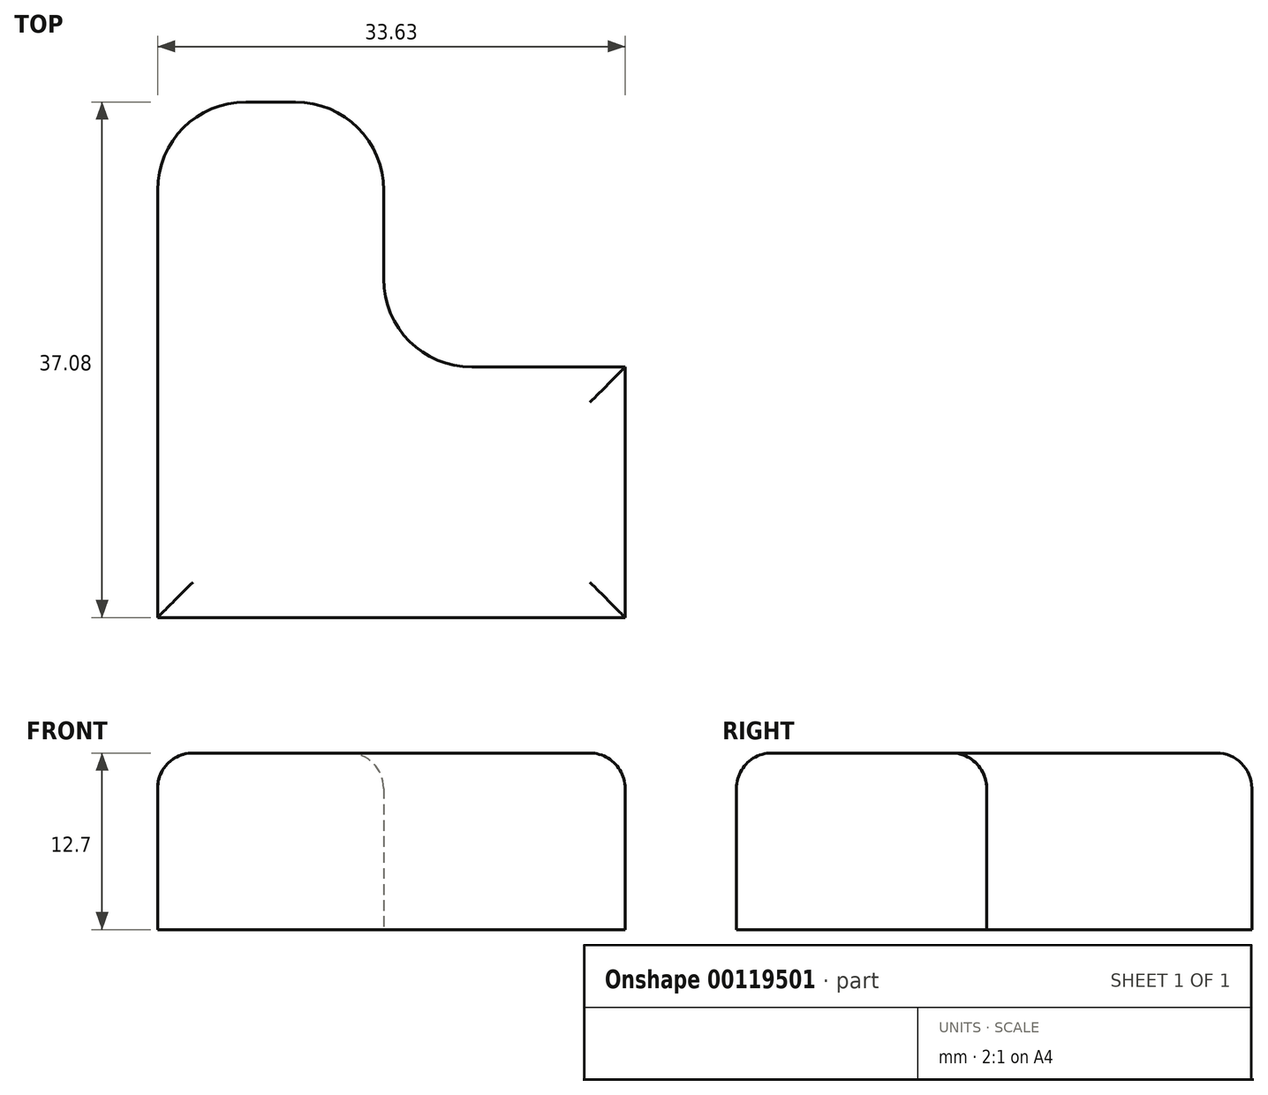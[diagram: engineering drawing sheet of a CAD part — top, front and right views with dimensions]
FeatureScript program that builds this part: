
annotation { "Feature Type Name" : "Feature", "Feature Type Description" : "" }
export const myFeature = defineFeature(function(context is Context, id is Id, definition is map)
    precondition{}
    {
        {
            var Q0;
            Q0=qCreatedBy(makeId("Top.planeOp"),FACE);
            var sketch = newSketch(context, id + "F0", { "sketchPlane" : qUnion([Q0])});
            skLineSegment(sketch, "E0", {"start": v(0, 0) * mm, "end": v(0, 30.73) * mm});
            skLineSegment(sketch, "E1", {"start": v(6.35, 37.08) * mm, "end": v(9.9, 37.08) * mm});
            skLineSegment(sketch, "E2", {"start": v(16.26, 30.73) * mm, "end": v(16.26, 24.36) * mm});
            skLineSegment(sketch, "E3", {"start": v(22.6, 18) * mm, "end": v(33.63, 18) * mm});
            skLineSegment(sketch, "E4", {"start": v(33.63, 18) * mm, "end": v(33.63, 0) * mm});
            skLineSegment(sketch, "E5", {"start": v(33.63, 0) * mm, "end": v(0, 0) * mm});
            skPoint(sketch, "E6.visualSharp", {"position": v(0, 37.08) * mm});
            skArc(sketch, "E6.filletArc", {"start": v(6.35, 37.08) * mm, "mid": v(1.86, 35.22) * mm, "end": v(0, 30.73) * mm});
            skPoint(sketch, "E7.visualSharp", {"position": v(16.26, 37.08) * mm});
            skArc(sketch, "E7.filletArc", {"start": v(16.26, 30.73) * mm, "mid": v(14.4, 35.22) * mm, "end": v(9.9, 37.08) * mm});
            skPoint(sketch, "E8.visualSharp", {"position": v(16.26, 18) * mm});
            skArc(sketch, "E8.filletArc", {"start": v(16.26, 24.36) * mm, "mid": v(18.12, 19.87) * mm, "end": v(22.6, 18) * mm});
            skSolve(sketch);
        }
        {
            var Q0;
            Q0=makeQuery(id+"F0.imprint","IMPRINT",FACE,{"disambiguationData":[TD([[makeQuery(id+"F0.imprint","IMPRINT",EDGE,{"derivedFrom":sQuery(id+"F0.wireOp",EDGE,"E0")}),-1.0]])]});
            extrude(context, id + "F1", {"entities" : qUnion([Q0]), "depth" : 12.7 * mm});
        }
        {
            var Q0;
            Q0=makeQuery(id+"F1.opExtrude","CAP_EDGE",EDGE,{"disambiguationData":[OSD([sQuery(id+"F0.wireOp",EDGE,"E6.filletArc")])],"isStart":false});
            var Q1;
            Q1=makeQuery(id+"F1.opExtrude","CAP_EDGE",EDGE,{"disambiguationData":[OSD([sQuery(id+"F0.wireOp",EDGE,"E1")])],"isStart":false});
            var Q2;
            Q2=makeQuery(id+"F1.opExtrude","CAP_EDGE",EDGE,{"disambiguationData":[OSD([sQuery(id+"F0.wireOp",EDGE,"E7.filletArc")])],"isStart":false});
            var Q3;
            Q3=makeQuery(id+"F1.opExtrude","CAP_EDGE",EDGE,{"disambiguationData":[OSD([sQuery(id+"F0.wireOp",EDGE,"E2")])],"isStart":false});
            var Q4;
            Q4=makeQuery(id+"F1.opExtrude","CAP_EDGE",EDGE,{"disambiguationData":[OSD([sQuery(id+"F0.wireOp",EDGE,"E8.filletArc")])],"isStart":false});
            var Q5;
            Q5=makeQuery(id+"F1.opExtrude","CAP_EDGE",EDGE,{"disambiguationData":[OSD([sQuery(id+"F0.wireOp",EDGE,"E3")])],"isStart":false});
            var Q6;
            Q6=makeQuery(id+"F1.opExtrude","CAP_EDGE",EDGE,{"disambiguationData":[OSD([sQuery(id+"F0.wireOp",EDGE,"E4")])],"isStart":false});
            var Q7;
            Q7=makeQuery(id+"F1.opExtrude","CAP_EDGE",EDGE,{"disambiguationData":[OSD([sQuery(id+"F0.wireOp",EDGE,"E5")])],"isStart":false});
            var Q8;
            Q8=makeQuery(id+"F1.opExtrude","CAP_EDGE",EDGE,{"disambiguationData":[OSD([sQuery(id+"F0.wireOp",EDGE,"E0")])],"isStart":false});
            fillet(context, id + "F2", {"entities" : qUnion([Q0, Q1, Q2, Q3, Q4, Q5, Q6, Q7, Q8]), "radius" : 2.54 * mm, "tangentPropagation" : true, "allowEdgeOverflow" : false});
        }
    });
